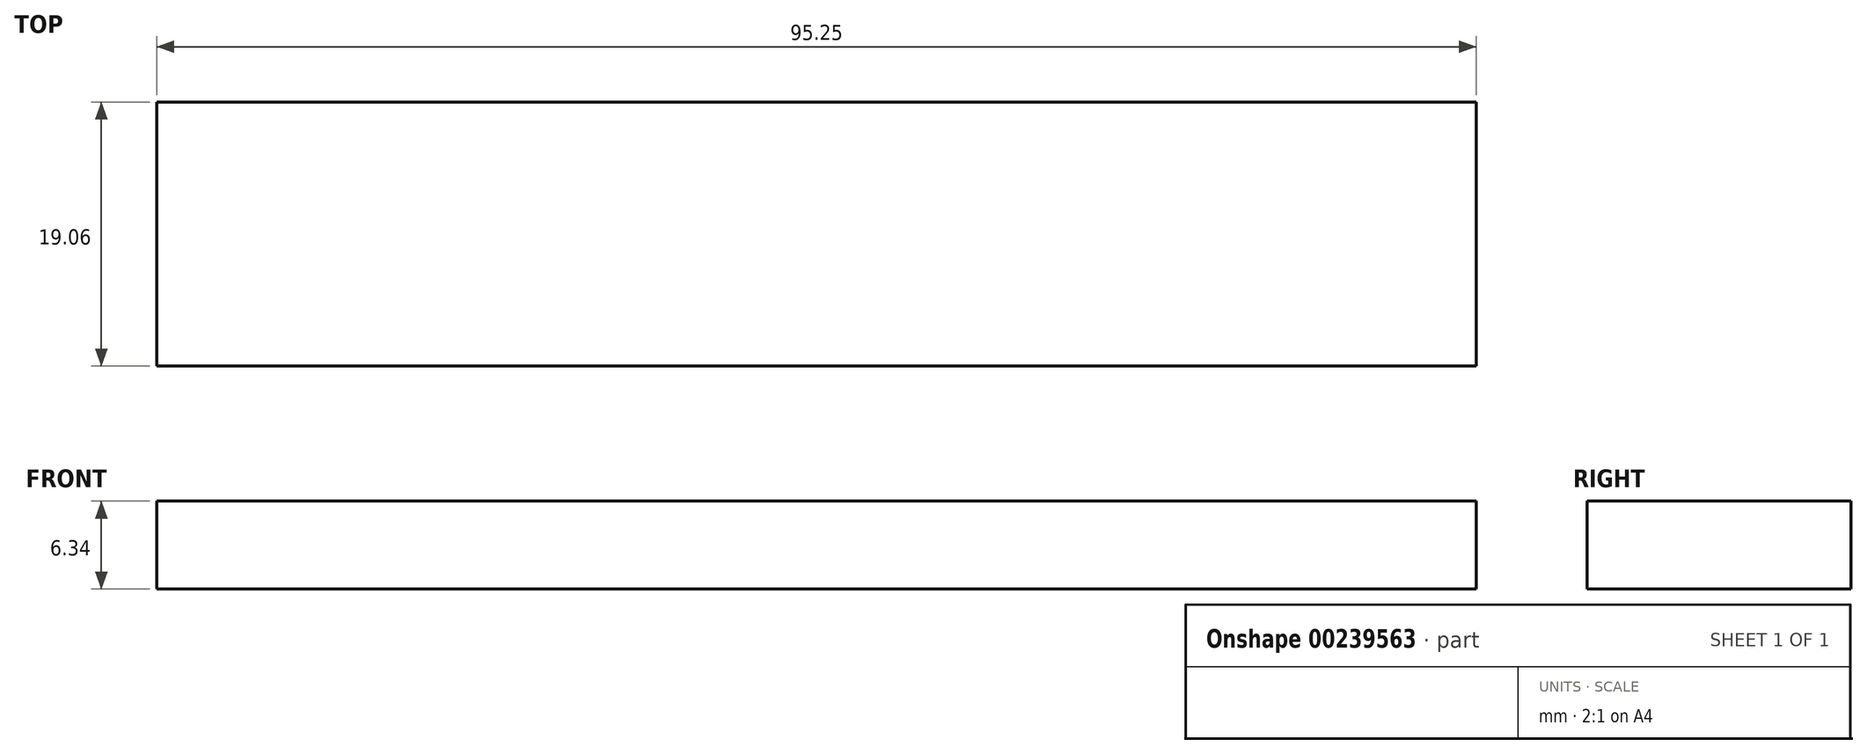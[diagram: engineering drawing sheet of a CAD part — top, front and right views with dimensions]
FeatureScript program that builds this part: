
annotation { "Feature Type Name" : "Feature", "Feature Type Description" : "" }
export const myFeature = defineFeature(function(context is Context, id is Id, definition is map)
    precondition{}
    {
        {
            var Q0;
            Q0=qCreatedBy(makeId("Front.planeOp"),FACE);
            var sketch = newSketch(context, id + "F0", { "sketchPlane" : qUnion([Q0])});
            skLineSegment(sketch, "E0.bottom", {"start": v(49.43, 3.18) * mm, "end": v(-45.82, 3.17) * mm});
            skLineSegment(sketch, "E0.top", {"start": v(49.43, -3.17) * mm, "end": v(-45.82, -3.18) * mm});
            skLineSegment(sketch, "E0.left", {"start": v(49.43, 3.18) * mm, "end": v(49.43, -3.17) * mm});
            skLineSegment(sketch, "E0.right", {"start": v(-45.82, 3.17) * mm, "end": v(-45.82, -3.18) * mm});
            skPoint(sketch, "E0.middle", {"position": v(1.8, 0) * mm});
            skSolve(sketch);
        }
        {
            var Q0;
            Q0 = qSketchRegion(id + "F0", true);
            extrude(context, id + "F1", {"entities" : qUnion([Q0]), "endBound" : BoundingType.SYMMETRIC, "depth" : 19.05 * mm});
        }
    });
